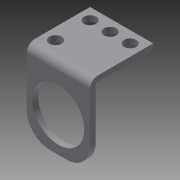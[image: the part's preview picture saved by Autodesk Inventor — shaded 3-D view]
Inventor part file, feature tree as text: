
AUTODESK INVENTOR PART (.ipt)
format: ipt  version: 2014 SP1 (Build 180222100, 222)  size: 214,528 bytes
history: native  units: in
note: dims shown in document units (in); Inventor stores cm internally (conversion verified against a paired STEP export)
features: other x6, sketch x5, sheet_metal_op x3, reference x1
ambient origin geometry x8: Origin, YZ Plane, XZ Plane, XY Plane, X Axis, Y Axis, Z Axis, Center Point
bodies: Solid1 (feature_tree)
feature tree (15):
  sheet_metal_op  "Face1"
  sheet_metal_op  "Flange1"
  sketch  "Sketch1"  dims[d0=1.3714in]
  other  "Plate1"
  sketch  "Sketch4"  dims[d2=1.25in]
  other  "Plate3"
  sheet_metal_op  "Bend2"
  sketch  "Sketch5"  dims[d3=0.266in]
  sketch  "Sketch6"  dims[d4=0.266in]
  sketch  "Sketch7"  dims[d5=0.4357in d6=0.266in d7=0.4357in d8=0.25in d9=0.25in d10=0.25in d11=0.25in d12=0.125in d28=0.125in d29=0.0625in d30=0.25in d31=0.125in d32=1.75in d33=90.0deg d34=0.05in d35=0.5in d36=0.125in d37=0.125in d38=1.125in d39=0.125in d40=0.0in d41=0.75in d43=0.0in d44=1.0in d47=1.0in d48=0.125in d49=0.0in d50=0.125in d51=0.0in d1=0.125in]
  reference  "Reference1"
  other  "Cut1"
  other  "Cut2"
  other  "Cut3"
  other  "Definition1"
